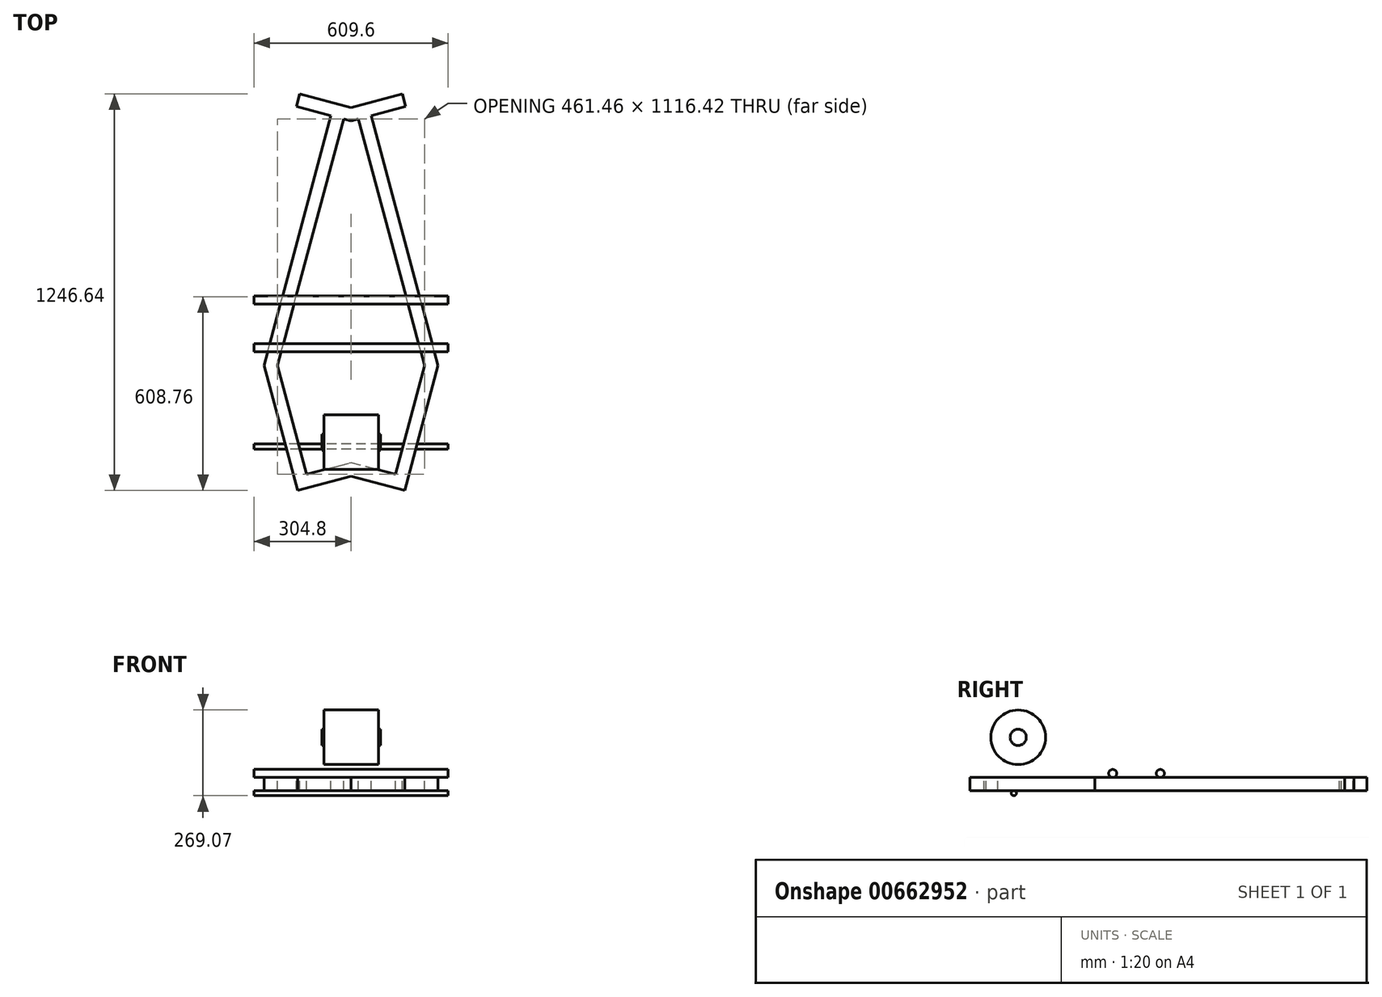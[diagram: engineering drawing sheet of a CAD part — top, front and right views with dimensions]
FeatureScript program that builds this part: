
annotation { "Feature Type Name" : "Feature", "Feature Type Description" : "" }
export const myFeature = defineFeature(function(context is Context, id is Id, definition is map)
    precondition{}
    {
        {
            var Q0;
            Q0=qCreatedBy(makeId("Top.planeOp"),FACE);
            var sketch = newSketch(context, id + "F0", { "sketchPlane" : qUnion([Q0])});
            skLineSegment(sketch, "E0", {"start": v(168.28, -392.55) * mm, "end": v(273.46, 0) * mm});
            skLineSegment(sketch, "E1", {"start": v(273.46, 0) * mm, "end": v(63.1, 785.1) * mm});
            skLineSegment(sketch, "E2", {"start": v(0, 768.2) * mm, "end": v(0, -580.23) * mm, "construction": true});
            skLineSegment(sketch, "E3.MirrorCS", {"start": v(-168.28, -392.55) * mm, "end": v(-273.46, 0) * mm});
            skLineSegment(sketch, "E4.MirrorCS", {"start": v(-273.46, 0) * mm, "end": v(-63.1, 785.1) * mm});
            skLineSegment(sketch, "E5", {"start": v(0, 768.2) * mm, "end": v(-171.74, 814.22) * mm});
            skLineSegment(sketch, "E6.MirrorCS", {"start": v(0, 768.2) * mm, "end": v(171.74, 814.22) * mm});
            skLineSegment(sketch, "E7", {"start": v(-168.27, -392.55) * mm, "end": v(0, -347.46) * mm});
            skLineSegment(sketch, "E8", {"start": v(0, -347.46) * mm, "end": v(168.28, -392.55) * mm});
            skLineSegment(sketch, "E9.0", {"start": v(0, 810.93) * mm, "end": v(-161.06, 854.09) * mm});
            skLineSegment(sketch, "E9.1", {"start": v(0, 810.93) * mm, "end": v(161.06, 854.09) * mm});
            skLineSegment(sketch, "E10", {"start": v(-161.06, 854.09) * mm, "end": v(-171.74, 814.22) * mm});
            skLineSegment(sketch, "E11", {"start": v(161.06, 854.09) * mm, "end": v(171.74, 814.22) * mm});
            skLineSegment(sketch, "E12.0", {"start": v(230.73, 0) * mm, "end": v(23.22, 774.42) * mm});
            skLineSegment(sketch, "E12.1", {"start": v(139.09, -342) * mm, "end": v(230.73, 0) * mm});
            skLineSegment(sketch, "E12.2", {"start": v(-230.73, 0) * mm, "end": v(-23.22, 774.42) * mm});
            skLineSegment(sketch, "E12.3", {"start": v(-139.09, -342) * mm, "end": v(-230.73, 0) * mm});
            skLineSegment(sketch, "E12.4", {"start": v(-139.09, -342) * mm, "end": v(0, -304.73) * mm});
            skLineSegment(sketch, "E12.5", {"start": v(0, -304.73) * mm, "end": v(139.09, -342) * mm});
            skSolve(sketch);
        }
        {
            var Q0;
            Q0=qCreatedBy(makeId("Front.planeOp"),FACE);
            var sketch = newSketch(context, id + "F1", { "sketchPlane" : qUnion([Q0])});
            skLineSegment(sketch, "E13", {"start": v(-229, 12.7) * mm, "end": v(-229, 15.88) * mm});
            skLineSegment(sketch, "E14", {"start": v(-235.36, 22.23) * mm, "end": v(-267.1, 22.23) * mm});
            skLineSegment(sketch, "E15", {"start": v(-273.46, 15.88) * mm, "end": v(-273.46, -15.88) * mm});
            skLineSegment(sketch, "E16", {"start": v(-352.61, 0) * mm, "end": v(-131.56, 0) * mm, "construction": true});
            skLineSegment(sketch, "E17.MirrorCS", {"start": v(-229, -12.7) * mm, "end": v(-229, -15.88) * mm});
            skLineSegment(sketch, "E18.MirrorCS", {"start": v(-235.36, -22.22) * mm, "end": v(-267.1, -22.22) * mm});
            skPoint(sketch, "E19.visualSharp", {"position": v(-229, 22.23) * mm});
            skArc(sketch, "E19.filletArc", {"start": v(-229, 15.88) * mm, "mid": v(-230.87, 20.37) * mm, "end": v(-235.36, 22.23) * mm});
            skPoint(sketch, "E20.visualSharp", {"position": v(-273.46, 22.23) * mm});
            skArc(sketch, "E20.filletArc", {"start": v(-267.1, 22.23) * mm, "mid": v(-271.6, 20.37) * mm, "end": v(-273.46, 15.88) * mm});
            skPoint(sketch, "E21.visualSharp", {"position": v(-273.46, -22.23) * mm});
            skArc(sketch, "E21.filletArc", {"start": v(-273.46, -15.88) * mm, "mid": v(-271.6, -20.37) * mm, "end": v(-267.1, -22.23) * mm});
            skPoint(sketch, "E22.visualSharp", {"position": v(-229, -22.23) * mm});
            skArc(sketch, "E22.filletArc", {"start": v(-235.36, -22.23) * mm, "mid": v(-230.87, -20.37) * mm, "end": v(-229, -15.88) * mm});
            skLineSegment(sketch, "E23.0", {"start": v(-235.36, -12.7) * mm, "end": v(-235.36, -15.88) * mm});
            skLineSegment(sketch, "E23.1", {"start": v(-235.36, 12.7) * mm, "end": v(-235.36, 15.88) * mm});
            skLineSegment(sketch, "E23.2", {"start": v(-235.36, 15.88) * mm, "end": v(-267.1, 15.88) * mm});
            skLineSegment(sketch, "E23.3", {"start": v(-267.1, 15.88) * mm, "end": v(-267.1, -15.88) * mm});
            skLineSegment(sketch, "E23.4", {"start": v(-235.36, -15.88) * mm, "end": v(-267.1, -15.88) * mm});
            skLineSegment(sketch, "E24", {"start": v(-235.36, 12.7) * mm, "end": v(-229, 12.7) * mm});
            skLineSegment(sketch, "E25", {"start": v(-235.36, -12.7) * mm, "end": v(-229, -12.7) * mm});
            skSolve(sketch);
        }
        {
            var Q0;
            Q0 = qSketchRegion(id + "F0", true);
            extrude(context, id + "F2", {"entities" : qUnion([Q0]), "oppositeDirection" : true, "depth" : 41.27 * mm, "offsetDistance" : 25.4 * mm});
        }
        {
            var Q0;
            Q0=qCreatedBy(makeId("Right.planeOp"),FACE);
            var sketch = newSketch(context, id + "F3", { "sketchPlane" : qUnion([Q0])});
            skCircle(sketch, "E26", {"center": v(-254.64, -49.21) * mm, "radius": 7.94 * mm});
            skCircle(sketch, "E27", {"center": v(205.59, 12.7) * mm, "radius": 12.7 * mm});
            skCircle(sketch, "E28", {"center": v(-240.86, 126.2) * mm, "radius": 85.73 * mm});
            skCircle(sketch, "E29", {"center": v(56.02, 12.7) * mm, "radius": 12.7 * mm});
            skCircle(sketch, "E30", {"center": v(-240.86, 126.2) * mm, "radius": 25.4 * mm});
            skSolve(sketch);
        }
        {
            var Q0;
            Q0=makeQuery(id+"F3.imprint","IMPRINT",FACE,{"disambiguationData":[TD([[makeQuery(id+"F3.imprint","IMPRINT",EDGE,{"derivedFrom":sQuery(id+"F3.wireOp",EDGE,"E28")}),1.0]])]});
            extrude(context, id + "F4", {"entities" : qUnion([Q0]), "endBound" : BoundingType.SYMMETRIC, "depth" : 171.45 * mm, "offsetDistance" : 25.4 * mm});
        }
        {
            var Q0;
            Q0=makeQuery(id+"F3.imprint","IMPRINT",FACE,{"disambiguationData":[TD([[makeQuery(id+"F3.imprint","IMPRINT",EDGE,{"derivedFrom":sQuery(id+"F3.wireOp",EDGE,"E30")}),1.0]])]});
            extrude(context, id + "F5", {"entities" : qUnion([Q0]), "operationType" : NewBodyOperationType.ADD, "endBound" : BoundingType.SYMMETRIC, "depth" : 184.15 * mm, "offsetDistance" : 25.4 * mm});
        }
        {
            var Q0;
            Q0=makeQuery(id+"F3.imprint","IMPRINT",FACE,{"disambiguationData":[TD([[makeQuery(id+"F3.imprint","IMPRINT",EDGE,{"derivedFrom":sQuery(id+"F3.wireOp",EDGE,"E27")}),1.0]])]});
            var Q1;
            Q1=makeQuery(id+"F3.imprint","IMPRINT",FACE,{"disambiguationData":[TD([[makeQuery(id+"F3.imprint","IMPRINT",EDGE,{"derivedFrom":sQuery(id+"F3.wireOp",EDGE,"E26")}),1.0]])]});
            var Q2;
            Q2=makeQuery(id+"F3.imprint","IMPRINT",FACE,{"disambiguationData":[TD([[makeQuery(id+"F3.imprint","IMPRINT",EDGE,{"derivedFrom":sQuery(id+"F3.wireOp",EDGE,"E29")}),1.0]])]});
            extrude(context, id + "F6", {"entities" : qUnion([Q0, Q1, Q2]), "operationType" : NewBodyOperationType.ADD, "endBound" : BoundingType.SYMMETRIC, "depth" : 609.6 * mm, "offsetDistance" : 25.4 * mm});
        }
    });
